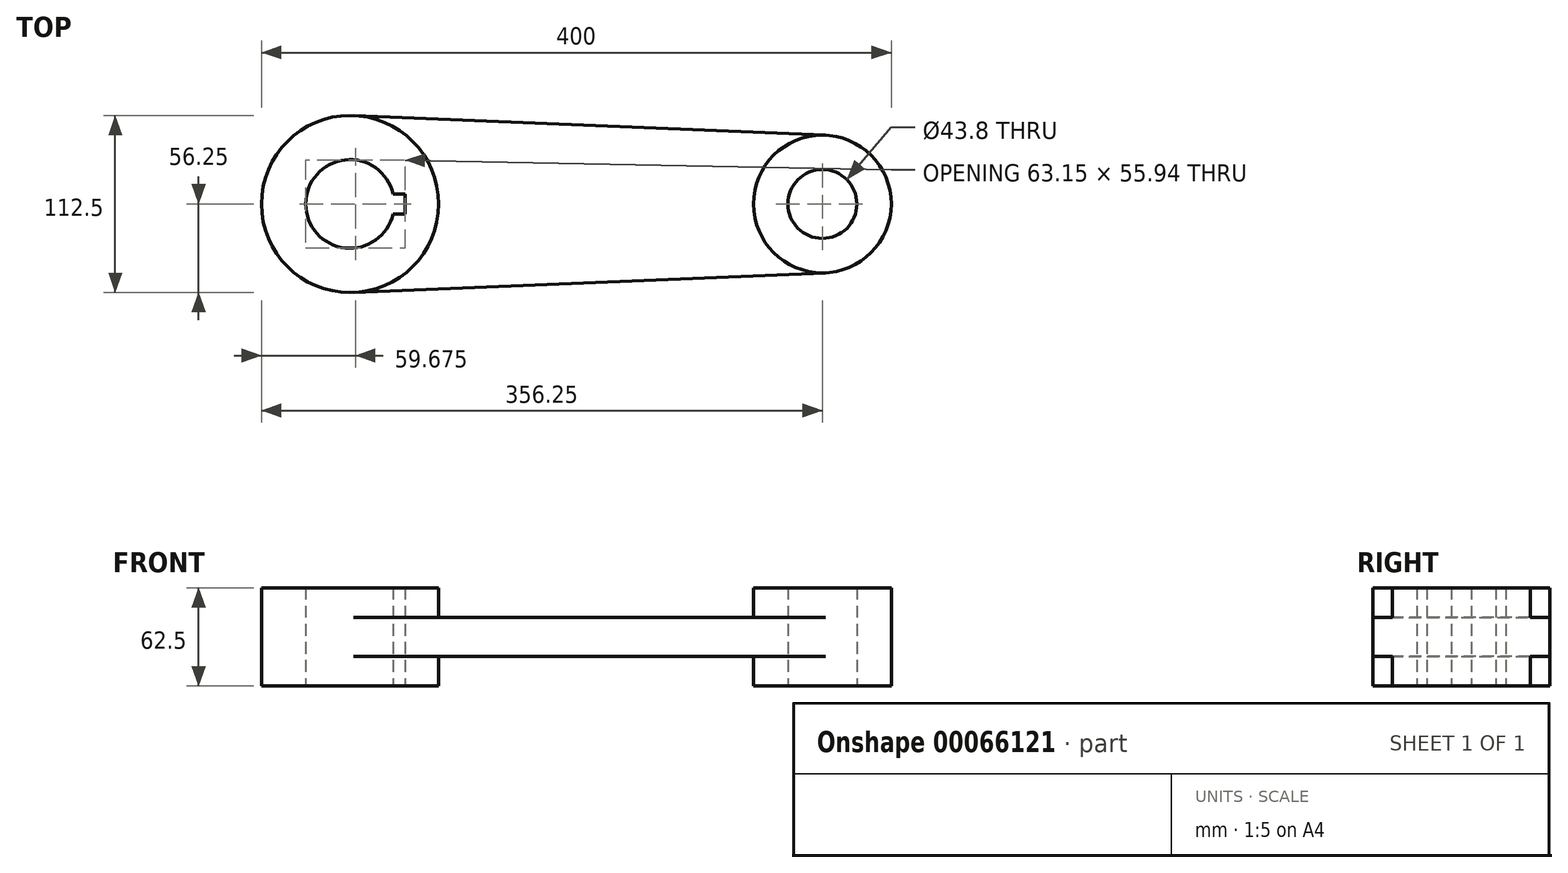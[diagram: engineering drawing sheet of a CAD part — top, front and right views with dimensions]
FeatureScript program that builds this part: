
annotation { "Feature Type Name" : "Feature", "Feature Type Description" : "" }
export const myFeature = defineFeature(function(context is Context, id is Id, definition is map)
    precondition{}
    {
        {
            var Q0;
            Q0=qCreatedBy(makeId("Top.planeOp"),FACE);
            var sketch = newSketch(context, id + "F0", { "sketchPlane" : qUnion([Q0])});
            skArc(sketch, "E0", {"start": v(-147.66, 56.2) * mm, "mid": v(-206.25, 0) * mm, "end": v(-147.66, -56.2) * mm});
            skArc(sketch, "E1", {"start": v(-122.56, 6.3) * mm, "mid": v(-178.15, 0) * mm, "end": v(-122.56, -6.3) * mm});
            skArc(sketch, "E2", {"start": v(151.82, -43.71) * mm, "mid": v(193.75, 0) * mm, "end": v(151.82, 43.71) * mm});
            skCircle(sketch, "E3", {"center": v(150, 0) * mm, "radius": 21.9 * mm});
            skLineSegment(sketch, "E4", {"start": v(-122.56, 6.3) * mm, "end": v(-115, 6.3) * mm});
            skLineSegment(sketch, "E5", {"start": v(-115, 6.3) * mm, "end": v(-115, -6.3) * mm});
            skLineSegment(sketch, "E6", {"start": v(-115, -6.3) * mm, "end": v(-122.56, -6.3) * mm});
            skLineSegment(sketch, "E7", {"start": v(-147.66, 56.2) * mm, "end": v(151.82, 43.71) * mm});
            skLineSegment(sketch, "E8", {"start": v(-147.66, -56.2) * mm, "end": v(151.82, -43.71) * mm});
            skSolve(sketch);
        }
        {
            var Q0;
            Q0=makeQuery(id+"F0.imprint","IMPRINT",FACE,{"disambiguationData":[TD([[makeQuery(id+"F0.imprint","IMPRINT",EDGE,{"derivedFrom":sQuery(id+"F0.wireOp",EDGE,"E0")}),1.0]])]});
            extrude(context, id + "F1", {"entities" : qUnion([Q0]), "depth" : 12.5 * mm, "hasSecondDirection" : true, "secondDirectionOppositeDirection" : true, "secondDirectionDepth" : 12.5 * mm});
        }
        {
            var Q0;
            Q0=makeQuery(id+"F1.opExtrude","CAP_FACE",FACE,{"disambiguationData":[OSD([sQuery(id+"F0.wireOp",EDGE,"E0"),sQuery(id+"F0.wireOp",EDGE,"E1"),sQuery(id+"F0.wireOp",EDGE,"E2"),sQuery(id+"F0.wireOp",EDGE,"E3"),sQuery(id+"F0.wireOp",EDGE,"E4"),sQuery(id+"F0.wireOp",EDGE,"E5"),sQuery(id+"F0.wireOp",EDGE,"E6"),sQuery(id+"F0.wireOp",EDGE,"E7"),sQuery(id+"F0.wireOp",EDGE,"E8")])],"isStart":false});
            var sketch = newSketch(context, id + "F2", { "sketchPlane" : qUnion([Q0])});
            skArc(sketch, "E9.0", {"start": v(-122.56, 6.3) * mm, "mid": v(-178.15, 0) * mm, "end": v(-122.56, -6.3) * mm});
            skLineSegment(sketch, "E10.0", {"start": v(-122.56, 6.3) * mm, "end": v(-115, 6.3) * mm});
            skLineSegment(sketch, "E11.0", {"start": v(-115, 6.3) * mm, "end": v(-115, -6.3) * mm});
            skLineSegment(sketch, "E12.0", {"start": v(-115, -6.3) * mm, "end": v(-122.56, -6.3) * mm});
            skCircle(sketch, "E13.0", {"center": v(150, 0) * mm, "radius": 21.9 * mm});
            skCircle(sketch, "E14", {"center": v(-150, 0) * mm, "radius": 56.25 * mm});
            skCircle(sketch, "E15", {"center": v(150, 0) * mm, "radius": 43.75 * mm});
            skSolve(sketch);
        }
        {
            var Q0;
            Q0=makeQuery(id+"F2.imprint","IMPRINT",FACE,{"disambiguationData":[TD([[makeQuery(id+"F2.imprint","IMPRINT",EDGE,{"derivedFrom":sQuery(id+"F2.wireOp",EDGE,"E9.0")}),-1.0]])]});
            var Q1;
            Q1=makeQuery(id+"F2.imprint","IMPRINT",FACE,{"disambiguationData":[TD([[makeQuery(id+"F2.imprint","IMPRINT",EDGE,{"derivedFrom":sQuery(id+"F2.wireOp",EDGE,"E13.0")}),-1.0]])]});
            extrude(context, id + "F3", {"entities" : qUnion([Q0, Q1]), "operationType" : NewBodyOperationType.ADD, "depth" : 18.75 * mm});
        }
        {
            var Q0;
            Q0=makeQuery(id+"F1.opExtrude","SWEPT_BODY",BODY,{"disambiguationData":[OSD([sQuery(id+"F0.wireOp",EDGE,"E0"),sQuery(id+"F0.wireOp",EDGE,"E1"),sQuery(id+"F0.wireOp",EDGE,"E2"),sQuery(id+"F0.wireOp",EDGE,"E3"),sQuery(id+"F0.wireOp",EDGE,"E4"),sQuery(id+"F0.wireOp",EDGE,"E5"),sQuery(id+"F0.wireOp",EDGE,"E6"),sQuery(id+"F0.wireOp",EDGE,"E7"),sQuery(id+"F0.wireOp",EDGE,"E8")])]});
            var Q1;
            Q1=qCreatedBy(makeId("Top.planeOp"),FACE);
            mirror(context, id + "F4", {"operationType" : NewBodyOperationType.ADD, "entities" : qUnion([Q0]), "mirrorPlane" : qUnion([Q1])});
        }
    });
